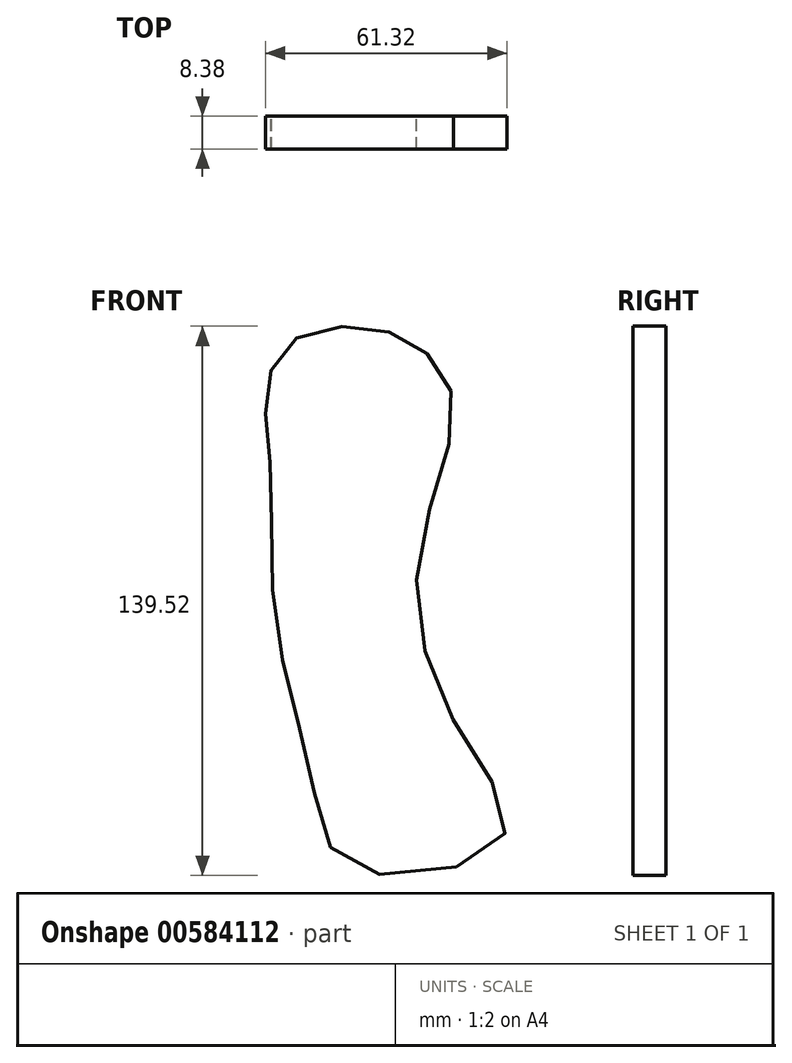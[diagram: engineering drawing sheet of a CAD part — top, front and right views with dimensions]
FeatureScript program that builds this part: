
annotation { "Feature Type Name" : "Feature", "Feature Type Description" : "" }
export const myFeature = defineFeature(function(context is Context, id is Id, definition is map)
    precondition{}
    {
        {
            var Q0;
            Q0=qCreatedBy(makeId("Front.planeOp"),FACE);
            var sketch = newSketch(context, id + "F0", { "sketchPlane" : qUnion([Q0])});
            skFitSpline(sketch, "E0", {"points": [v(-29.63, 52.1) * mm, v(-23.43, 65.26) * mm, v(-5.23, 69.13) * mm, v(10.65, 62.94) * mm, v(18, 47.45) * mm, v(9.1, 10.65) * mm, v(18.78, -32.34) * mm, v(30.4, -61) * mm, v(-7.17, -68.36) * mm, v(-18, -45.9) * mm, v(-27.3, -5.23) * mm, v(-28.47, 31.95) * mm, v(-29.63, 52.1) * mm]});
            skFitSpline(sketch, "E1", {"points": [v(8.6, 4.84) * mm, v(32.73, 9.1) * mm, v(19.56, 7.17) * mm], "startDerivative": vector(62.88, 10.85) * mm, "endDerivative": vector(-46.5, -7.1) * mm});
            skSolve(sketch);
        }
        {
            var Q0;
            Q0 = qSketchRegion(id + "F0", true);
            var Q1;
            Q1=makeQuery(id+"F0.imprint","IMPRINT",FACE,{"disambiguationData":[TD([[makeQuery(id+"F0.imprint","IMPRINT",EDGE,{"derivedFrom":sQuery(id+"F0.wireOp",EDGE,"E0")}),-1.0]])]});
            extrude(context, id + "F1", {"entities" : qUnion([Q0, Q1]), "depth" : 8.38 * mm, "offsetDistance" : 25.4 * mm});
        }
    });
